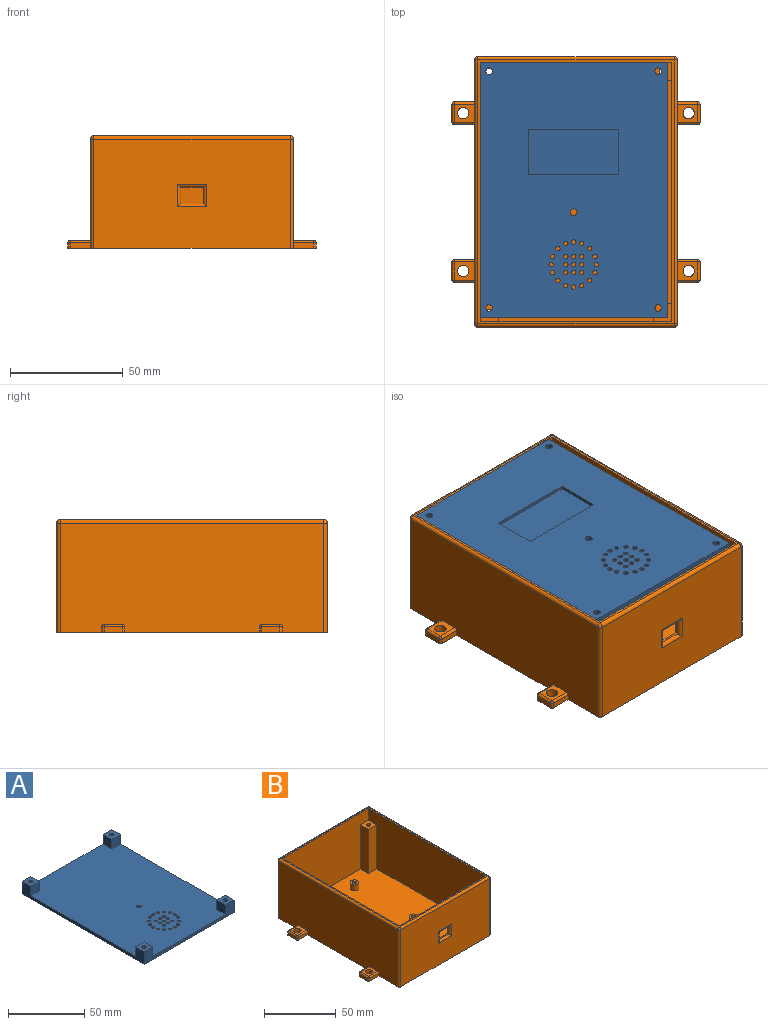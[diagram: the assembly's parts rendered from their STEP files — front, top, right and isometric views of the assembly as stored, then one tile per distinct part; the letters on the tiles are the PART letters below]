
ASSEMBLY  parts=2 mates=1
PART A: 53 faces, bbox 83x113x10 mm
  f0: plane 83x10mm, normal (0,1,0), area 327.5mm2, adj f1,f3,f4,f5,f8,f9,f10,f13
  f1: plane 113x10mm, normal (-1,0,0), area 402.5mm2, adj f0,f2,f4,f5,f6,f9,f16,f17
  f2: plane 83x10mm, normal (0,-1,0), area 327.5mm2, adj f1,f3,f4,f5,f14,f17,f18,f21
  f3: plane 113x10mm, normal (1,0,0), area 402.5mm2, adj f0,f2,f4,f5,f11,f13,f20,f21
  f4: plane 113x83mm, normal (0,0,1), area 9037.4mm2, adj f0,f1,f2,f3,f6,f8,f10,f11
  f5: plane 113x83mm, normal (0,0,-1), area 8465.1mm2, adj f0,f1,f2,f3,f7,f12,f15,f19
  f6: plane 8x7.5mm, normal (0,-1,0), area 60mm2, adj f1,f4,f8,f9
  f7: cylinder r=1.5mm len=10mm, axis (0,0,-1), area 94.2mm2, adj f5,f9
  f8: plane 8x7.5mm, normal (1,0,0), area 60mm2, adj f0,f4,f6,f9
  f9: plane 8x8mm, normal (0,0,1), area 56.9mm2, adj f0,f1,f6,f7,f8
  f10: plane 8x7.5mm, normal (-1,0,0), area 60mm2, adj f0,f4,f11,f13
  f11: plane 8x7.5mm, normal (0,-1,0), area 60mm2, adj f3,f4,f10,f13
  f12: cylinder r=1.5mm len=10mm, axis (0,0,-1), area 94.2mm2, adj f5,f13
  f13: plane 8x8mm, normal (0,0,1), area 56.9mm2, adj f0,f3,f10,f11,f12
  f14: plane 8x7.5mm, normal (1,0,0), area 60mm2, adj f2,f4,f16,f17
  f15: cylinder r=1.5mm len=10mm, axis (0,0,-1), area 94.2mm2, adj f5,f17
  f16: plane 8x7.5mm, normal (0,1,0), area 60mm2, adj f1,f4,f14,f17
  f17: plane 8x8mm, normal (0,0,1), area 56.9mm2, adj f1,f2,f14,f15,f16
  f18: plane 8x7.5mm, normal (-1,0,0), area 60mm2, adj f2,f4,f20,f21
  f19: cylinder r=1.5mm len=10mm, axis (0,0,-1), area 94.2mm2, adj f5,f21
  f20: plane 8x7.5mm, normal (0,1,0), area 60mm2, adj f3,f4,f18,f21
  f21: plane 8x8mm, normal (0,0,1), area 56.9mm2, adj f2,f3,f18,f19,f20
  f22: plane 40x1.5mm, normal (0,-1,0), area 60mm2, adj f5,f23,f25,f26
  f23: plane 20x1.5mm, normal (1,0,0), area 30mm2, adj f5,f22,f24,f26
  f24: plane 40x1.5mm, normal (0,1,0), area 60mm2, adj f5,f23,f25,f26
  f25: plane 20x1.5mm, normal (-1,0,0), area 30mm2, adj f5,f22,f24,f26
  f26: plane 40x20mm, normal (0,0,-1), area 800mm2, adj f22,f23,f24,f25
  f27: cylinder r=1mm len=2.5mm, axis (0,0,1), area 15.7mm2, adj f4,f5
  f28: cylinder r=1mm len=2.5mm, axis (0,0,1), area 15.7mm2, adj f4,f5
  f29: cylinder r=1mm len=2.5mm, axis (0,0,1), area 15.7mm2, adj f4,f5
  f30: cylinder r=1mm len=2.5mm, axis (0,0,1), area 15.7mm2, adj f4,f5
  f31: cylinder r=1mm len=2.5mm, axis (0,0,1), area 15.7mm2, adj f4,f5
  f32: cylinder r=1mm len=2.5mm, axis (0,0,1), area 15.7mm2, adj f4,f5
  f33: cylinder r=1mm len=2.5mm, axis (0,0,1), area 15.7mm2, adj f4,f5
  f34: cylinder r=1mm len=2.5mm, axis (0,0,1), area 15.7mm2, adj f4,f5
  f35: cylinder r=1mm len=2.5mm, axis (0,0,1), area 15.7mm2, adj f4,f5
  f36: cylinder r=1mm len=2.5mm, axis (0,0,1), area 15.7mm2, adj f4,f5
  f37: cylinder r=1mm len=2.5mm, axis (0,0,1), area 15.7mm2, adj f4,f5
  f38: cylinder r=1mm len=2.5mm, axis (0,0,1), area 15.7mm2, adj f4,f5
  f39: cylinder r=1mm len=2.5mm, axis (0,0,1), area 15.7mm2, adj f4,f5
  f40: cylinder r=1mm len=2.5mm, axis (0,0,1), area 15.7mm2, adj f4,f5
  f41: cylinder r=1mm len=2.5mm, axis (0,0,1), area 15.7mm2, adj f4,f5
  f42: cylinder r=1mm len=2.5mm, axis (0,0,1), area 15.7mm2, adj f4,f5
  f43: cylinder r=1mm len=2.5mm, axis (0,0,1), area 15.7mm2, adj f4,f5
  f44: cylinder r=1mm len=2.5mm, axis (0,0,1), area 15.7mm2, adj f4,f5
  f45: cylinder r=1mm len=2.5mm, axis (0,0,1), area 15.7mm2, adj f4,f5
  f46: cylinder r=1mm len=2.5mm, axis (0,0,1), area 15.7mm2, adj f4,f5
  f47: cylinder r=1mm len=2.5mm, axis (0,0,1), area 15.7mm2, adj f4,f5
  f48: cylinder r=1mm len=2.5mm, axis (0,0,1), area 15.7mm2, adj f4,f5
  f49: cylinder r=1mm len=2.5mm, axis (0,0,1), area 15.7mm2, adj f4,f5
  f50: cylinder r=1mm len=2.5mm, axis (0,0,1), area 15.7mm2, adj f4,f5
  f51: cylinder r=1mm len=2.5mm, axis (0,0,1), area 15.7mm2, adj f4,f5
  f52: cylinder r=1.5mm len=3mm, axis (0,0,1), area 23.6mm2, adj f4,f5
PART B: 119 faces, bbox 110x120x50 mm
  f0: plane 87x48.5mm, normal (0,-1,0), area 4089.5mm2, adj f12,f15,f17,f18,f99,f100,f101,f102
  f1: plane 85x47.5mm, normal (0,1,0), area 3367.5mm2, adj f6,f9,f13,f14,f82,f83,f85,f86
  f2: cylinder r=2.5mm len=38mm, axis (0,0,-1), area 596.9mm2, adj f12,f94
  f3: cylinder r=2.5mm len=38mm, axis (0,0,-1), area 596.9mm2, adj f12,f92
  f4: cylinder r=2.5mm len=38mm, axis (0,0,-1), area 596.9mm2, adj f12,f90
  f5: cylinder r=2.5mm len=38mm, axis (0,0,-1), area 596.9mm2, adj f12,f88
  f6: plane 115x47.5mm, normal (-1,0,0), area 4862.5mm2, adj f1,f7,f9,f14,f78,f80,f84,f86
  f7: plane 85x47.5mm, normal (0,-1,0), area 3437.5mm2, adj f6,f9,f13,f14,f76,f77,f79,f80
  f8: plane 117x48.5mm, normal (-1,0,0), area 5605.4mm2, adj f12,f15,f19,f20,f27,f30,f31,f32
  f9: plane 117x87mm, normal (0,0,1), area 404mm2, adj f1,f6,f7,f13,f18,f19,f23,f24
  f10: plane 117x48.5mm, normal (1,0,0), area 5605.4mm2, adj f12,f17,f23,f26,f37,f38,f41,f42
  f11: plane 87x48.5mm, normal (0,1,0), area 4219.5mm2, adj f12,f20,f24,f26
  f12: plane 120x110mm, normal (0,0,-1), area 11039.3mm2, adj f0,f2,f3,f4,f5,f8,f10,f11
  f13: plane 115x47.5mm, normal (1,0,0), area 4862.5mm2, adj f1,f7,f9,f14,f75,f77,f81,f83
  f14: plane 115x85mm, normal (0,0,1), area 9398.2mm2, adj f1,f6,f7,f13,f75,f76,f78,f79
  f15: cylinder r=1.5mm len=48.5mm, axis (0,0,-1), area 114.3mm2, adj f0,f8,f12,f16
  f16: sphere r=1.5mm, area 3.5mm2, adj f15,f18,f19
  f17: cylinder r=1.5mm len=48.5mm, axis (0,0,1), area 114.3mm2, adj f0,f10,f12,f21
  f18: cylinder r=1.5mm len=87mm, axis (-1,0,0), area 205mm2, adj f0,f9,f16,f21
  f19: cylinder r=1.5mm len=117mm, axis (0,1,0), area 275.7mm2, adj f8,f9,f16,f22
  f20: cylinder r=1.5mm len=48.5mm, axis (0,0,1), area 114.3mm2, adj f8,f11,f12,f22
  f21: sphere r=1.5mm, area 3.5mm2, adj f17,f18,f23
  f22: sphere r=1.5mm, area 3.5mm2, adj f19,f20,f24
  f23: cylinder r=1.5mm len=117mm, axis (0,-1,0), area 275.7mm2, adj f9,f10,f21,f25
  f24: cylinder r=1.5mm len=87mm, axis (1,0,0), area 205mm2, adj f9,f11,f22,f25
  f25: sphere r=1.5mm, area 3.5mm2, adj f23,f24,f26
  f26: cylinder r=1.5mm len=48.5mm, axis (0,0,-1), area 114.3mm2, adj f10,f11,f12,f25
  f27: plane 9x2.5mm, normal (0,1,0), area 22.5mm2, adj f8,f12,f64,f67
  f28: plane 8x2.5mm, normal (-1,0,0), area 20mm2, adj f12,f62,f65,f67
  f29: cylinder r=2.5mm len=5mm, axis (0,0,-1), area 55mm2, adj f12,f31
  f30: plane 9x2.5mm, normal (0,-1,0), area 22.5mm2, adj f8,f12,f61,f62
  f31: plane 9x8mm, normal (0,0,1), area 52.4mm2, adj f8,f29,f61,f64,f65
  f32: plane 9x2.5mm, normal (0,1,0), area 22.5mm2, adj f8,f12,f68,f69
  f33: plane 8x2.5mm, normal (-1,0,0), area 20mm2, adj f12,f68,f71,f74
  f34: cylinder r=2.5mm len=5mm, axis (0,0,-1), area 55mm2, adj f12,f36
  f35: plane 9x2.5mm, normal (0,-1,0), area 22.5mm2, adj f8,f12,f72,f74
  f36: plane 9x8mm, normal (0,0,1), area 52.4mm2, adj f8,f34,f69,f71,f72
  f37: plane 9x2.5mm, normal (0,1,0), area 22.5mm2, adj f10,f12,f51,f53
  f38: plane 9x2.5mm, normal (0,-1,0), area 22.5mm2, adj f10,f12,f47,f48
  f39: cylinder r=2.5mm len=5mm, axis (0,0,-1), area 55mm2, adj f12,f41
  f40: plane 8x2.5mm, normal (1,0,0), area 20mm2, adj f12,f47,f50,f53
  f41: plane 9x8mm, normal (0,0,1), area 52.4mm2, adj f10,f39,f48,f50,f51
  f42: plane 9x2.5mm, normal (0,1,0), area 22.5mm2, adj f10,f12,f58,f60
  f43: plane 9x2.5mm, normal (0,-1,0), area 22.5mm2, adj f10,f12,f54,f55
  f44: cylinder r=2.5mm len=5mm, axis (0,0,-1), area 55mm2, adj f12,f46
  f45: plane 8x2.5mm, normal (1,0,0), area 20mm2, adj f12,f54,f57,f60
  f46: plane 9x8mm, normal (0,0,1), area 52.4mm2, adj f10,f44,f55,f57,f58
  f47: cylinder r=1mm len=2.5mm, axis (0,0,1), area 3.9mm2, adj f12,f38,f40,f49
  f48: cylinder r=1mm len=9mm, axis (-1,0,0), area 14.1mm2, adj f10,f38,f41,f49
  f49: sphere r=1mm, area 1.6mm2, adj f47,f48,f50
  f50: cylinder r=1mm len=8mm, axis (0,-1,0), area 12.6mm2, adj f40,f41,f49,f52
  f51: cylinder r=1mm len=9mm, axis (1,0,0), area 14.1mm2, adj f10,f37,f41,f52
  f52: sphere r=1mm, area 1.6mm2, adj f50,f51,f53
  f53: cylinder r=1mm len=2.5mm, axis (0,0,-1), area 3.9mm2, adj f12,f37,f40,f52
  f54: cylinder r=1mm len=2.5mm, axis (0,0,1), area 3.9mm2, adj f12,f43,f45,f56
  f55: cylinder r=1mm len=9mm, axis (-1,0,0), area 14.1mm2, adj f10,f43,f46,f56
  f56: sphere r=1mm, area 1.6mm2, adj f54,f55,f57
  f57: cylinder r=1mm len=8mm, axis (0,-1,0), area 12.6mm2, adj f45,f46,f56,f59
  f58: cylinder r=1mm len=9mm, axis (1,0,0), area 14.1mm2, adj f10,f42,f46,f59
  f59: sphere r=1mm, area 1.6mm2, adj f57,f58,f60
  f60: cylinder r=1mm len=2.5mm, axis (0,0,-1), area 3.9mm2, adj f12,f42,f45,f59
  f61: cylinder r=1mm len=9mm, axis (-1,0,0), area 14.1mm2, adj f8,f30,f31,f63
  f62: cylinder r=1mm len=2.5mm, axis (0,0,1), area 3.9mm2, adj f12,f28,f30,f63
  f63: sphere r=1mm, area 1.6mm2, adj f61,f62,f65
  f64: cylinder r=1mm len=9mm, axis (1,0,0), area 14.1mm2, adj f8,f27,f31,f66
  f65: cylinder r=1mm len=8mm, axis (0,1,0), area 12.6mm2, adj f28,f31,f63,f66
  f66: sphere r=1mm, area 1.6mm2, adj f64,f65,f67
  f67: cylinder r=1mm len=2.5mm, axis (0,0,-1), area 3.9mm2, adj f12,f27,f28,f66
  f68: cylinder r=1mm len=2.5mm, axis (0,0,-1), area 3.9mm2, adj f12,f32,f33,f70
  f69: cylinder r=1mm len=9mm, axis (1,0,0), area 14.1mm2, adj f8,f32,f36,f70
  f70: sphere r=1mm, area 1.6mm2, adj f68,f69,f71
  f71: cylinder r=1mm len=8mm, axis (0,1,0), area 12.6mm2, adj f33,f36,f70,f73
  f72: cylinder r=1mm len=9mm, axis (-1,0,0), area 14.1mm2, adj f8,f35,f36,f73
  f73: sphere r=1mm, area 1.6mm2, adj f71,f72,f74
  f74: cylinder r=1mm len=2.5mm, axis (0,0,1), area 3.9mm2, adj f12,f33,f35,f73
  f75: plane 37.5x8mm, normal (0,-1,0), area 300mm2, adj f13,f14,f76,f77
  f76: plane 37.5x8mm, normal (1,0,0), area 300mm2, adj f7,f14,f75,f77
  f77: plane 8x8mm, normal (0,0,1), area 56.9mm2, adj f7,f13,f75,f76,f89
  f78: plane 37.5x8mm, normal (0,-1,0), area 300mm2, adj f6,f14,f79,f80
  f79: plane 37.5x8mm, normal (-1,0,0), area 300mm2, adj f7,f14,f78,f80
  f80: plane 8x8mm, normal (0,0,1), area 56.9mm2, adj f6,f7,f78,f79,f87
  f81: plane 37.5x8mm, normal (0,1,0), area 300mm2, adj f13,f14,f82,f83
  f82: plane 37.5x8mm, normal (1,0,0), area 300mm2, adj f1,f14,f81,f83
  f83: plane 8x8mm, normal (0,0,1), area 56.9mm2, adj f1,f13,f81,f82,f93
  f84: plane 37.5x8mm, normal (0,1,0), area 300mm2, adj f6,f14,f85,f86
  f85: plane 37.5x8mm, normal (-1,0,0), area 300mm2, adj f1,f14,f84,f86
  f86: plane 8x8mm, normal (0,0,1), area 56.9mm2, adj f1,f6,f84,f85,f91
  f87: cylinder r=1.5mm len=3mm, axis (0,0,1), area 18.8mm2, adj f80,f88
  f88: plane 5x5mm, normal (0,0,-1), area 12.6mm2, adj f5,f87
  f89: cylinder r=1.5mm len=3mm, axis (0,0,1), area 18.8mm2, adj f77,f90
  f90: plane 5x5mm, normal (0,0,-1), area 12.6mm2, adj f4,f89
  f91: cylinder r=1.5mm len=3mm, axis (0,0,1), area 18.8mm2, adj f86,f92
  f92: plane 5x5mm, normal (0,0,-1), area 12.6mm2, adj f3,f91
  f93: cylinder r=1.5mm len=3mm, axis (0,0,1), area 18.8mm2, adj f83,f94
  f94: plane 5x5mm, normal (0,0,-1), area 12.6mm2, adj f2,f93
  f95: plane 10x1mm, normal (0,0,1), area 10mm2, adj f1,f96,f98,f102
  f96: plane 7x1mm, normal (1,0,0), area 7mm2, adj f1,f95,f97,f100
  f97: plane 10x1mm, normal (0,0,-1), area 10mm2, adj f1,f96,f98,f99
  f98: plane 7x1mm, normal (-1,0,0), area 7mm2, adj f1,f95,f97,f101
  f99: cylinder r=1.5mm len=13mm, axis (1,0,0), area 26.1mm2, adj f0,f97,f100,f101
  f100: cylinder r=1.5mm len=10mm, axis (0,0,1), area 19.1mm2, adj f0,f96,f99,f102
  f101: cylinder r=1.5mm len=10mm, axis (0,0,-1), area 19.1mm2, adj f0,f98,f99,f102
  f102: cylinder r=1.5mm len=13mm, axis (-1,0,0), area 26.1mm2, adj f0,f95,f100,f101
  f103: cylinder r=1.38mm len=5mm, axis (0,0,-1), area 43.2mm2, adj f105,f106
  f104: cylinder r=3.1mm len=6.2mm, axis (0,0,-1), area 97.4mm2, adj f14,f105
  f105: plane 6.2x6.2mm, normal (0,0,1), area 24.3mm2, adj f103,f104
  f106: plane 2.75x2.75mm, normal (0,0,1), area 5.9mm2, adj f103
  f107: cylinder r=1.38mm len=5mm, axis (0,0,-1), area 43.2mm2, adj f109,f110
  f108: cylinder r=3.1mm len=6.2mm, axis (0,0,-1), area 97.4mm2, adj f14,f109
  f109: plane 6.2x6.2mm, normal (0,0,1), area 24.3mm2, adj f107,f108
  f110: plane 2.75x2.75mm, normal (0,0,1), area 5.9mm2, adj f107
  f111: cylinder r=1.38mm len=5mm, axis (0,0,-1), area 43.2mm2, adj f113,f114
  f112: cylinder r=3.1mm len=6.2mm, axis (0,0,-1), area 97.4mm2, adj f14,f113
  f113: plane 6.2x6.2mm, normal (0,0,1), area 24.3mm2, adj f111,f112
  f114: plane 2.75x2.75mm, normal (0,0,1), area 5.9mm2, adj f111
  f115: cylinder r=1.38mm len=5mm, axis (0,0,-1), area 43.2mm2, adj f117,f118
  f116: cylinder r=3.1mm len=6.2mm, axis (0,0,-1), area 97.4mm2, adj f14,f117
  f117: plane 6.2x6.2mm, normal (0,0,1), area 24.3mm2, adj f115,f116
  f118: plane 2.75x2.75mm, normal (0,0,1), area 5.9mm2, adj f115
PLACE A rot(axis=(0,1,0),180deg) t=(2.18,2.48,47.96)mm
PLACE B t=(-0.32,8.45,-2.04)mm fixed
MATE slider A.f12 <-> B.f4  axis (0,0,-1) through (-38.82,61.95,37.96)mm
